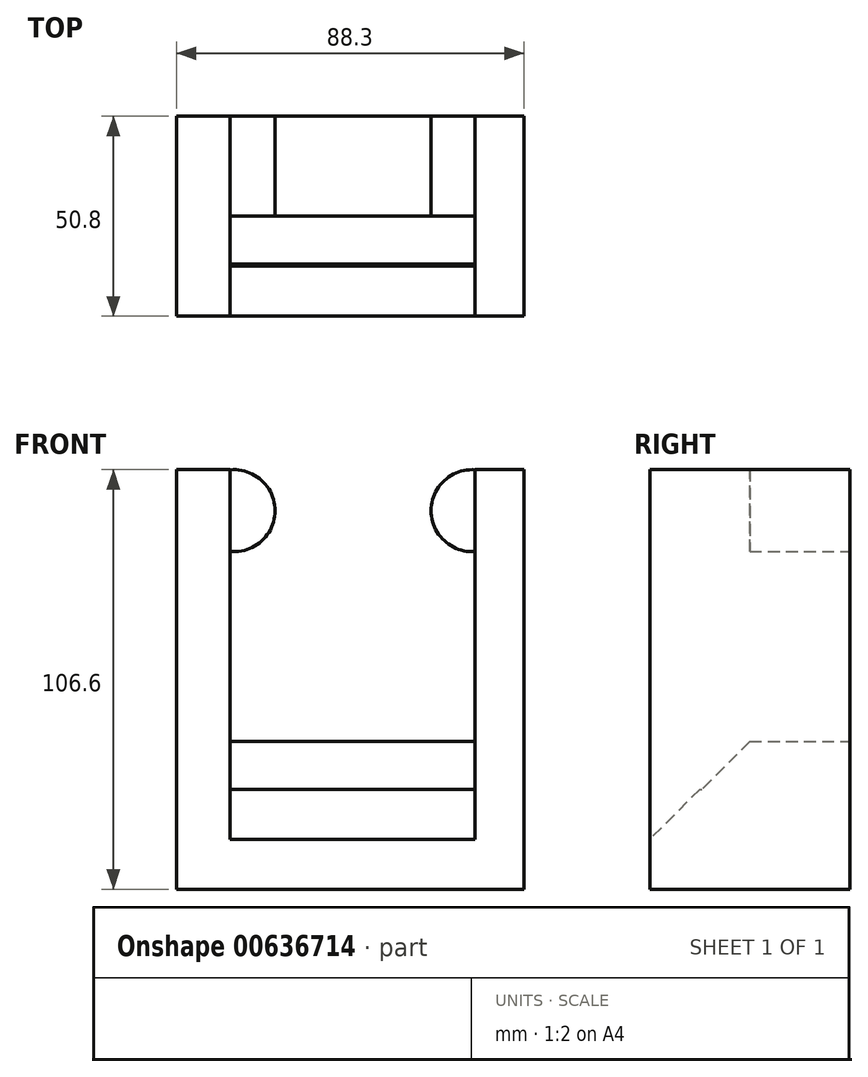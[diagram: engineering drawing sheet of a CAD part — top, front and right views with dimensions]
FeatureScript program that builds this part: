
annotation { "Feature Type Name" : "Feature", "Feature Type Description" : "" }
export const myFeature = defineFeature(function(context is Context, id is Id, definition is map)
    precondition{}
    {
        {
            var Q0;
            Q0=qCreatedBy(makeId("Front.planeOp"),FACE);
            var sketch = newSketch(context, id + "F0", { "sketchPlane" : qUnion([Q0])});
            skLineSegment(sketch, "E0", {"start": v(-44.93, 40.75) * mm, "end": v(-44.93, -40.45) * mm});
            skLineSegment(sketch, "E1", {"start": v(-44.93, -40.45) * mm, "end": v(43.37, -40.45) * mm});
            skLineSegment(sketch, "E2", {"start": v(43.37, -40.45) * mm, "end": v(43.37, 40.75) * mm});
            skLineSegment(sketch, "E3", {"start": v(43.37, 40.75) * mm, "end": v(30.97, 40.75) * mm});
            skLineSegment(sketch, "E4", {"start": v(30.97, 40.75) * mm, "end": v(30.97, -28.3) * mm});
            skLineSegment(sketch, "E5", {"start": v(30.97, -28.3) * mm, "end": v(-31.26, -28.3) * mm});
            skLineSegment(sketch, "E6", {"start": v(-31.26, -28.3) * mm, "end": v(-31.26, 40.75) * mm});
            skLineSegment(sketch, "E7", {"start": v(-31.26, 40.75) * mm, "end": v(-44.93, 40.75) * mm});
            skSolve(sketch);
        }
        {
            var Q0;
            Q0 = qSketchRegion(id + "F0", true);
            extrude(context, id + "F1", {"entities" : qUnion([Q0]), "depth" : 50.8 * mm, "offsetDistance" : 25.4 * mm});
        }
        {
            var Q0;
            Q0=qCreatedBy(makeId("Front.planeOp"),FACE);
            var sketch = newSketch(context, id + "F2", { "sketchPlane" : qUnion([Q0])});
            skCircle(sketch, "E8", {"center": v(-30.27, 30.34) * mm, "radius": 10.4 * mm});
            skCircle(sketch, "E9", {"center": v(30.2, 30.34) * mm, "radius": 10.4 * mm});
            skSolve(sketch);
        }
        {
            var Q0;
            Q0 = qSketchRegion(id + "F2", true);
            extrude(context, id + "F3", {"entities" : qUnion([Q0]), "operationType" : NewBodyOperationType.ADD, "depth" : 25.4 * mm, "offsetDistance" : 25.4 * mm});
        }
        {
            var Q0;
            Q0=makeQuery(id+"F1.opExtrude","CAP_EDGE",EDGE,{"disambiguationData":[OSD([sQuery(id+"F0.wireOp",EDGE,"E5")])],"isStart":false});
            chamfer(context, id + "F4", {"entities" : qUnion([Q0]), "width" : 25.4 * mm, "tangentPropagation" : true});
        }
        {
            var Q0;
            Q0=makeQuery(id+"F1.opExtrude","SWEPT_FACE",FACE,{"disambiguationData":[OSD([sQuery(id+"F0.wireOp",EDGE,"E1")])]});
            var sketch = newSketch(context, id + "F5", { "sketchPlane" : qUnion([Q0])});
            skLineSegment(sketch, "E10.bottom", {"start": v(-44.93, 50.8) * mm, "end": v(43.37, 50.8) * mm});
            skLineSegment(sketch, "E10.top", {"start": v(-44.93, 0) * mm, "end": v(43.37, 0) * mm});
            skLineSegment(sketch, "E10.left", {"start": v(-44.93, 50.8) * mm, "end": v(-44.93, 0) * mm});
            skLineSegment(sketch, "E10.right", {"start": v(43.37, 50.8) * mm, "end": v(43.37, 0) * mm});
            skSolve(sketch);
        }
        {
            var Q0;
            Q0 = qSketchRegion(id + "F5", true);
            extrude(context, id + "F6", {"entities" : qUnion([Q0]), "operationType" : NewBodyOperationType.ADD, "depth" : 25.4 * mm, "offsetDistance" : 25.4 * mm});
        }
        {
            var Q0;
            Q0=makeQuery(id+"F6.opExtrude","CAP_EDGE",EDGE,{"disambiguationData":[OSD([sQuery(id+"F5.wireOp",EDGE,"E10.bottom")])],"isStart":true});
            chamfer(context, id + "F7", {"entities" : qUnion([Q0]), "width" : 12.7 * mm, "tangentPropagation" : true});
        }
    });
